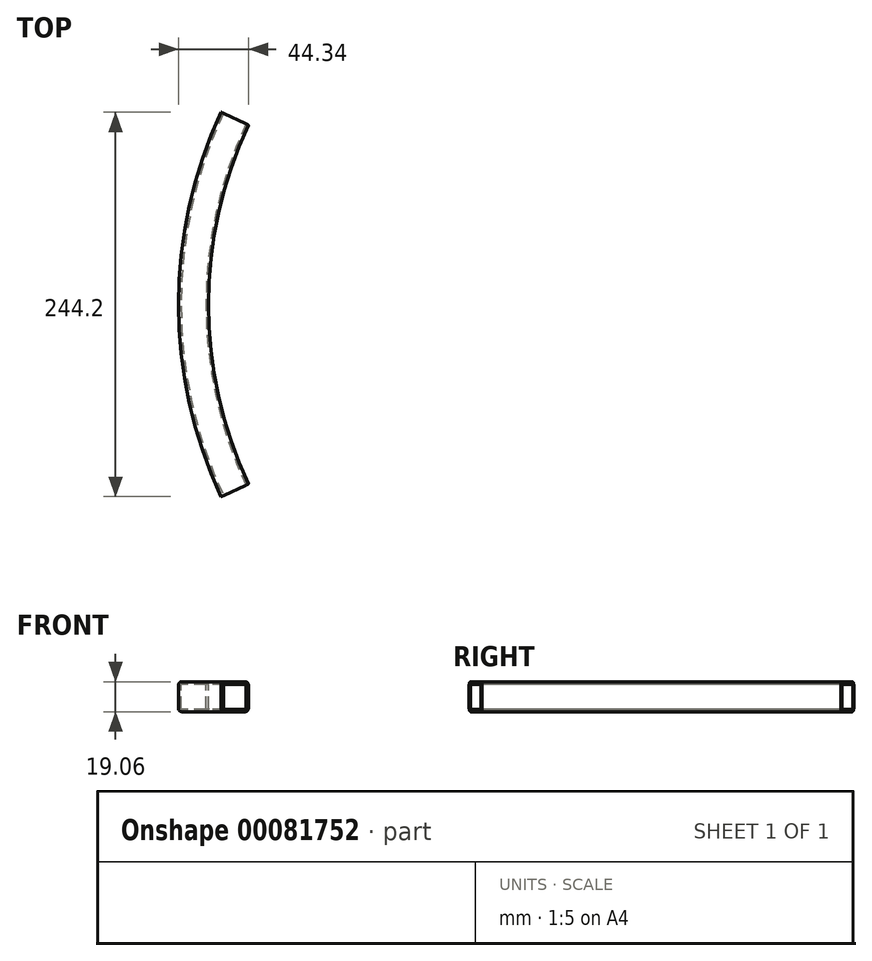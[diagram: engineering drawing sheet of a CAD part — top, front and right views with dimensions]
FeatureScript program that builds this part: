
annotation { "Feature Type Name" : "Feature", "Feature Type Description" : "" }
export const myFeature = defineFeature(function(context is Context, id is Id, definition is map)
    precondition{}
    {
        {
            var Q0;
            Q0=qCreatedBy(makeId("Front.planeOp"),FACE);
            var sketch = newSketch(context, id + "F0", { "sketchPlane" : qUnion([Q0])});
            skLineSegment(sketch, "E0.bottom", {"start": v(7.44, -9.52) * mm, "end": v(-7.44, -9.53) * mm});
            skLineSegment(sketch, "E0.top", {"start": v(7.44, 9.53) * mm, "end": v(-7.44, 9.52) * mm});
            skLineSegment(sketch, "E0.left", {"start": v(9.53, -7.44) * mm, "end": v(9.53, 7.44) * mm});
            skLineSegment(sketch, "E0.right", {"start": v(-9.53, -7.44) * mm, "end": v(-9.53, 7.44) * mm});
            skPoint(sketch, "E0.middle", {"position": v(0, 0) * mm});
            skLineSegment(sketch, "E1.bottom", {"start": v(7.44, -7.95) * mm, "end": v(-7.44, -7.95) * mm});
            skLineSegment(sketch, "E1.top", {"start": v(7.44, 7.95) * mm, "end": v(-7.44, 7.95) * mm});
            skLineSegment(sketch, "E1.left", {"start": v(7.95, -7.44) * mm, "end": v(7.95, 7.44) * mm});
            skLineSegment(sketch, "E1.right", {"start": v(-7.95, -7.44) * mm, "end": v(-7.95, 7.44) * mm});
            skPoint(sketch, "E2.visualSharp", {"position": v(-7.95, 7.95) * mm});
            skArc(sketch, "E2.filletArc", {"start": v(-7.44, 7.95) * mm, "mid": v(-7.8, 7.8) * mm, "end": v(-7.95, 7.44) * mm});
            skPoint(sketch, "E3.visualSharp", {"position": v(7.95, 7.95) * mm});
            skArc(sketch, "E3.filletArc", {"start": v(7.95, 7.44) * mm, "mid": v(7.8, 7.8) * mm, "end": v(7.44, 7.95) * mm});
            skPoint(sketch, "E4.visualSharp", {"position": v(7.95, -7.95) * mm});
            skArc(sketch, "E4.filletArc", {"start": v(7.44, -7.95) * mm, "mid": v(7.8, -7.8) * mm, "end": v(7.95, -7.44) * mm});
            skPoint(sketch, "E5.visualSharp", {"position": v(-7.95, -7.95) * mm});
            skArc(sketch, "E5.filletArc", {"start": v(-7.95, -7.44) * mm, "mid": v(-7.8, -7.8) * mm, "end": v(-7.44, -7.95) * mm});
            skPoint(sketch, "E6.visualSharp", {"position": v(9.53, 9.53) * mm});
            skArc(sketch, "E6.filletArc", {"start": v(9.53, 7.44) * mm, "mid": v(8.91, 8.91) * mm, "end": v(7.44, 9.53) * mm});
            skPoint(sketch, "E7.visualSharp", {"position": v(-9.53, 9.52) * mm});
            skArc(sketch, "E7.filletArc", {"start": v(-7.44, 9.53) * mm, "mid": v(-8.91, 8.91) * mm, "end": v(-9.53, 7.44) * mm});
            skPoint(sketch, "E8.visualSharp", {"position": v(-9.53, -9.53) * mm});
            skArc(sketch, "E8.filletArc", {"start": v(-9.53, -7.44) * mm, "mid": v(-8.91, -8.91) * mm, "end": v(-7.44, -9.52) * mm});
            skPoint(sketch, "E9.visualSharp", {"position": v(9.53, -9.52) * mm});
            skArc(sketch, "E9.filletArc", {"start": v(7.44, -9.52) * mm, "mid": v(8.91, -8.91) * mm, "end": v(9.52, -7.44) * mm});
            skLineSegment(sketch, "E10", {"start": v(279.4, 11.9) * mm, "end": v(279.4, -19.7) * mm});
            skSolve(sketch);
        }
        {
            var Q0;
            Q0=qSketchRegion(id+"F0",true);
            var Q1;
            Q1=sQuery(id+"F0.wireOp",EDGE,"E10");
            revolve(context, id + "F1", {"entities" : qUnion([Q0]), "axis" : qUnion([Q1]), "revolveType" : RevolveType.SYMMETRIC, "angle" : 50 * degree});
        }
    });
